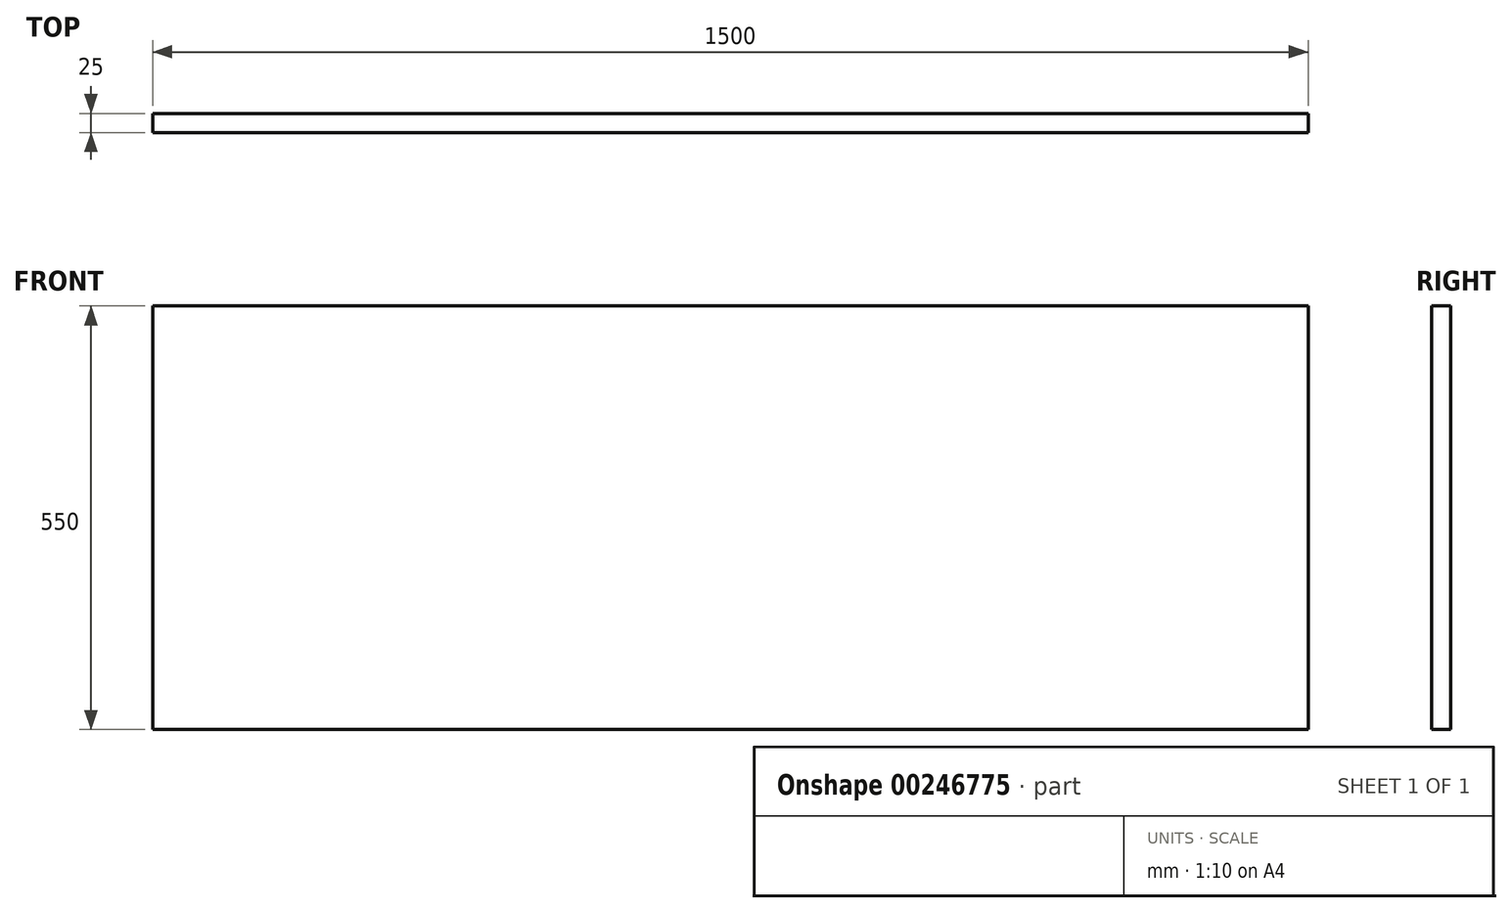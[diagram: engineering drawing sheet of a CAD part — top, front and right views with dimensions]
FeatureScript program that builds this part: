
annotation { "Feature Type Name" : "Feature", "Feature Type Description" : "" }
export const myFeature = defineFeature(function(context is Context, id is Id, definition is map)
    precondition{}
    {
        {
            var Q0;
            Q0=qCreatedBy(makeId("Front.planeOp"),FACE);
            var sketch = newSketch(context, id + "F0", { "sketchPlane" : qUnion([Q0])});
            skLineSegment(sketch, "E0.bottom", {"start": v(-744.28, 205.03) * mm, "end": v(755.72, 205.03) * mm});
            skLineSegment(sketch, "E0.top", {"start": v(-744.28, -344.97) * mm, "end": v(755.72, -344.97) * mm});
            skLineSegment(sketch, "E0.left", {"start": v(-744.28, 205.03) * mm, "end": v(-744.28, -344.97) * mm});
            skLineSegment(sketch, "E0.right", {"start": v(755.72, 205.03) * mm, "end": v(755.72, -344.97) * mm});
            skSolve(sketch);
        }
        {
            var Q0;
            Q0=makeQuery(id+"F0.imprint","IMPRINT",FACE,{"disambiguationData":[TD([[makeQuery(id+"F0.imprint","IMPRINT",EDGE,{"derivedFrom":sQuery(id+"F0.wireOp",EDGE,"E0.bottom")}),-1.0]])]});
            extrude(context, id + "F1", {"entities" : qUnion([Q0]), "depth" : 25 * mm});
        }
    });
